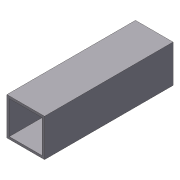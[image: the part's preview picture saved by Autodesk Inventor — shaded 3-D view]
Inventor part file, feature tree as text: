
AUTODESK INVENTOR PART (.ipt)
format: ipt  version: 2012 (Build 160160000, 160)  size: 72,192 bytes
history: native  units: in
note: dims shown in document units (in); Inventor stores cm internally (conversion verified against a paired STEP export)
features: extrude x1, shell x1, sketch x1
ambient origin geometry x8: Origin, YZ Plane, XZ Plane, XY Plane, X Axis, Y Axis, Z Axis, Center Point
bodies: Solid1 (feature_tree)
feature tree (3):
  extrude  "Extrusion1"  Depth=1.0in
  shell  "Shell2"  Thickness=3.42in
  sketch  "Sketch1"  dims[d0=1.0in d1=1.0in d2=3.42in d3=0.0in d5=0.0625in]
